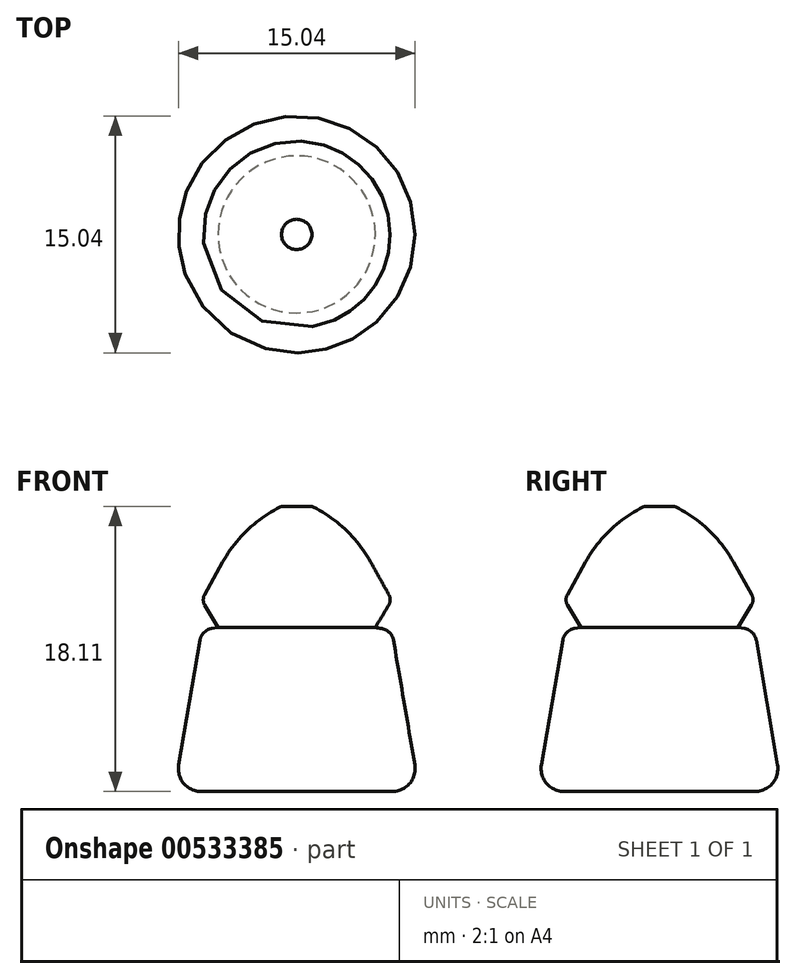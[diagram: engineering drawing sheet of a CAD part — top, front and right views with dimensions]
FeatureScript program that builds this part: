
annotation { "Feature Type Name" : "Feature", "Feature Type Description" : "" }
export const myFeature = defineFeature(function(context is Context, id is Id, definition is map)
    precondition{}
    {
        {
            var Q0;
            Q0=qCreatedBy(makeId("Front.planeOp"),FACE);
            var sketch = newSketch(context, id + "F0", { "sketchPlane" : qUnion([Q0])});
            skLineSegment(sketch, "E0", {"start": v(0, 0) * mm, "end": v(-7.79, 0) * mm});
            skLineSegment(sketch, "E1", {"start": v(-7.79, 0) * mm, "end": v(-6.04, 10.24) * mm});
            skLineSegment(sketch, "E2", {"start": v(-6.04, 10.24) * mm, "end": v(-4.99, 10.41) * mm});
            skLineSegment(sketch, "E3", {"start": v(-4.99, 10.41) * mm, "end": v(-6.04, 12.16) * mm});
            skLineSegment(sketch, "E4", {"start": v(-6.04, 12.16) * mm, "end": v(-3.41, 16.89) * mm});
            skLineSegment(sketch, "E5", {"start": v(-3.41, 16.89) * mm, "end": v(-0.96, 18.11) * mm});
            skLineSegment(sketch, "E6", {"start": v(-0.96, 18.11) * mm, "end": v(0, 18.11) * mm});
            skLineSegment(sketch, "E7", {"start": v(0, 18.11) * mm, "end": v(0, 0) * mm});
            skSolve(sketch);
        }
        {
            var Q0;
            Q0 = qSketchRegion(id + "F0", true);
            var Q1;
            Q1=sQuery(id+"F0.wireOp",EDGE,"E7");
            revolve(context, id + "F1", {"entities" : qUnion([Q0]), "axis" : qUnion([Q1]), "revolveType" : RevolveType.FULL});
        }
        {
            var Q0;
            Q0=makeQuery(id+"F1.opRevolve","SWEPT_EDGE",EDGE,{"disambiguationData":[OSD([sQuery(id+"F0.wireOp",EDGE,"E4"),sQuery(id+"F0.wireOp",EDGE,"E5")])]});
            fillet(context, id + "F2", {"entities" : qUnion([Q0]), "radius" : 8.55 * mm, "tangentPropagation" : true, "allowEdgeOverflow" : false});
        }
        {
            var Q0;
            Q0=makeQuery(id+"F1.opRevolve","SWEPT_EDGE",EDGE,{"disambiguationData":[OSD([sQuery(id+"F0.wireOp",EDGE,"E3"),sQuery(id+"F0.wireOp",EDGE,"E4")])]});
            fillet(context, id + "F3", {"entities" : qUnion([Q0]), "radius" : 0.65 * mm, "tangentPropagation" : true, "allowEdgeOverflow" : false});
        }
        {
            var Q0;
            Q0=makeQuery(id+"F1.opRevolve","SWEPT_EDGE",EDGE,{"disambiguationData":[OSD([sQuery(id+"F0.wireOp",EDGE,"E1"),sQuery(id+"F0.wireOp",EDGE,"E2")])]});
            fillet(context, id + "F4", {"entities" : qUnion([Q0]), "radius" : 0.88 * mm, "tangentPropagation" : true, "allowEdgeOverflow" : false});
        }
        {
            var Q0;
            Q0=makeQuery(id+"F1.opRevolve","SWEPT_EDGE",EDGE,{"disambiguationData":[OSD([sQuery(id+"F0.wireOp",EDGE,"E0"),sQuery(id+"F0.wireOp",EDGE,"E1")])]});
            fillet(context, id + "F5", {"entities" : qUnion([Q0]), "radius" : 1.45 * mm, "tangentPropagation" : true, "allowEdgeOverflow" : false});
        }
    });
